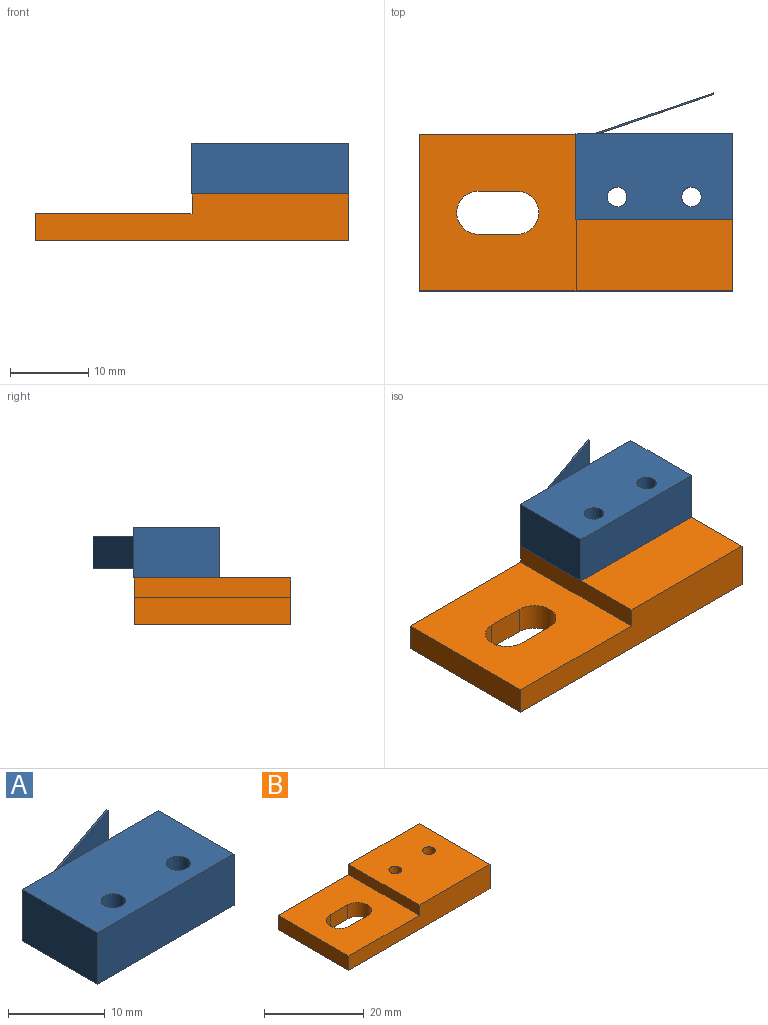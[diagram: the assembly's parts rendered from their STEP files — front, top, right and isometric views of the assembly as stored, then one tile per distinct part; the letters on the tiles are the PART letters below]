
ASSEMBLY  parts=2 mates=1
PART A: 13 faces, bbox 20x16.2x6.5 mm
  f0: plane 20x6.5mm, normal (0,1,0), area 127.5mm2, adj f1,f3,f6,f7,f8,f9,f11,f12
  f1: plane 11x6.5mm, normal (-1,0,0), area 71.5mm2, adj f0,f2,f6,f7
  f2: plane 20x6.5mm, normal (0,-1,0), area 130mm2, adj f1,f3,f6,f7
  f3: plane 11x6.5mm, normal (1,0,0), area 71.5mm2, adj f0,f2,f6,f7
  f4: cylinder r=1.25mm len=6.5mm, axis (0,0,-1), area 51.1mm2, adj f6,f7
  f5: cylinder r=1.25mm len=6.5mm, axis (0,0,-1), area 51.1mm2, adj f6,f7
  f6: plane 20x11mm, normal (0,0,1), area 210.2mm2, adj f0,f1,f2,f3,f4,f5
  f7: plane 20x11mm, normal (0,0,-1), area 210.2mm2, adj f0,f1,f2,f3,f4,f5
  f8: plane 15.14x5.19mm, normal (-0.32,0.95,0), area 64mm2, adj f0,f10,f11,f12
  f9: plane 14.58x5mm, normal (0.32,-0.95,0), area 61.7mm2, adj f0,f10,f11,f12
  f10: plane 4x0.19mm, normal (0.95,0.32,0), area 0.8mm2, adj f8,f9,f11,f12
  f11: plane 15.2x5.19mm, normal (0,0,1), area 3.1mm2, adj f0,f8,f9,f10
  f12: plane 15.2x5.19mm, normal (0,0,-1), area 3.1mm2, adj f0,f8,f9,f10
PART B: 28 faces, bbox 40x20x6 mm
  f0: plane 40x20mm, normal (0,0,-1), area 703.7mm2, adj f3,f4,f5,f6,f7,f8,f9,f10
  f1: plane 20x20mm, normal (0,0,1), area 389.4mm2, adj f4,f5,f10,f11,f12,f13
  f2: plane 20x20mm, normal (0,0,1), area 348.7mm2, adj f3,f4,f6,f7,f8,f9,f10,f11
  f3: plane 20x3.5mm, normal (-1,0,0), area 70mm2, adj f0,f2,f4,f10
  f4: plane 40x6mm, normal (0,-1,0), area 190mm2, adj f0,f1,f2,f3,f5,f11
  f5: plane 20x6mm, normal (1,0,0), area 120mm2, adj f0,f1,f4,f10
  f6: cylinder r=2.75mm len=5.5mm, axis (0,0,-1), area 30.2mm2, adj f0,f2,f7,f9
  f7: plane 5x3.5mm, normal (0,-1,0), area 17.5mm2, adj f0,f2,f6,f8
  f8: cylinder r=2.75mm len=5.5mm, axis (0,0,-1), area 30.2mm2, adj f0,f2,f7,f9
  f9: plane 5x3.5mm, normal (0,1,0), area 17.5mm2, adj f0,f2,f6,f8
  f10: plane 40x6mm, normal (0,1,0), area 190mm2, adj f0,f1,f2,f3,f5,f11
  f11: plane 20x2.5mm, normal (-1,0,0), area 50mm2, adj f1,f2,f4,f10
  f12: cylinder r=1.3mm len=3.5mm, axis (0,0,-1), area 28.6mm2, adj f1,f20
  f13: cylinder r=1.3mm len=3.5mm, axis (0,0,-1), area 28.6mm2, adj f1,f27
  f14: plane 2.55x2.5mm, normal (0.5,0.87,0), area 7.4mm2, adj f0,f15,f19,f20
  f15: plane 2.55x2.5mm, normal (-0.5,0.87,0), area 7.4mm2, adj f0,f14,f16,f20
  f16: plane 2.94x2.5mm, normal (-1,0,0), area 7.4mm2, adj f0,f15,f17,f20
  f17: plane 2.55x2.5mm, normal (-0.5,-0.87,0), area 7.4mm2, adj f0,f16,f18,f20
  f18: plane 2.55x2.5mm, normal (0.5,-0.87,0), area 7.4mm2, adj f0,f17,f19,f20
  f19: plane 2.94x2.5mm, normal (1,0,0), area 7.4mm2, adj f0,f14,f18,f20
  f20: plane 5.89x5.1mm, normal (0,0,-1), area 17.2mm2, adj f12,f14,f15,f16,f17,f18,f19
  f21: plane 2.55x2.5mm, normal (-0.5,-0.87,0), area 7.4mm2, adj f0,f22,f26,f27
  f22: plane 2.55x2.5mm, normal (0.5,-0.87,0), area 7.4mm2, adj f0,f21,f23,f27
  f23: plane 2.94x2.5mm, normal (1,0,0), area 7.4mm2, adj f0,f22,f24,f27
  f24: plane 2.55x2.5mm, normal (0.5,0.87,0), area 7.4mm2, adj f0,f23,f25,f27
  f25: plane 2.55x2.5mm, normal (-0.5,0.87,0), area 7.4mm2, adj f0,f24,f26,f27
  f26: plane 2.94x2.5mm, normal (-1,0,0), area 7.4mm2, adj f0,f21,f25,f27
  f27: plane 5.89x5.1mm, normal (0,0,-1), area 17.2mm2, adj f13,f21,f22,f23,f24,f25,f26
PLACE A t=(10.49,12.45,9.82)mm
PLACE B t=(-9.51,-26.65,3.82)mm
MATE fastened B.f12 <-> A.f5  axis (0,0,-1) through (25.24,15.35,9.82)mm
